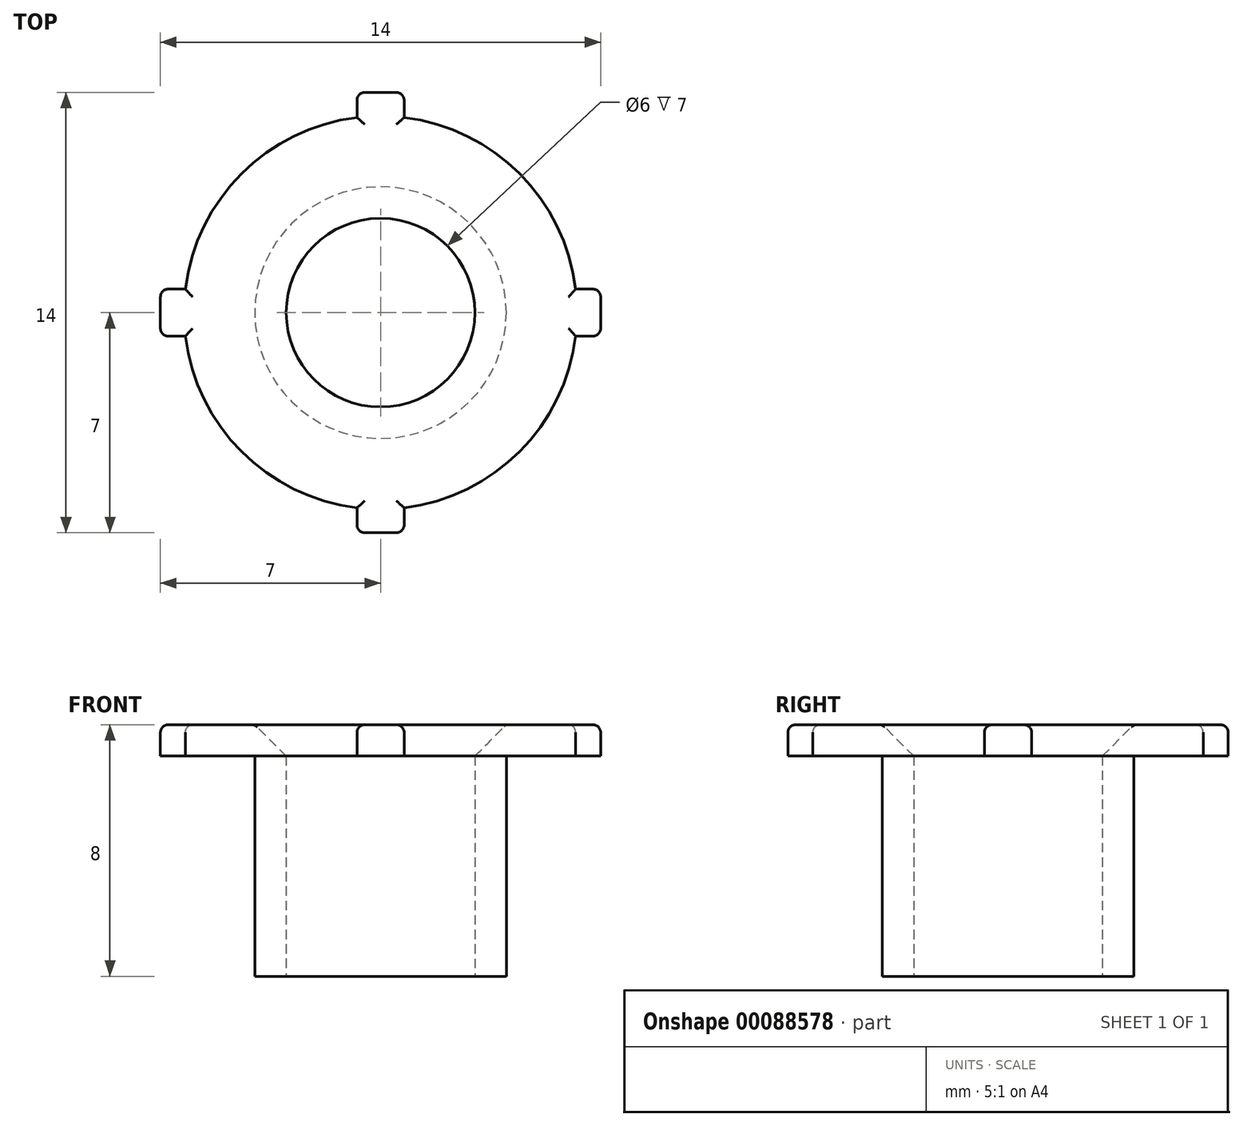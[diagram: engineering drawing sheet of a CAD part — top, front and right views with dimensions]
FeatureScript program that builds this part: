
annotation { "Feature Type Name" : "Feature", "Feature Type Description" : "" }
export const myFeature = defineFeature(function(context is Context, id is Id, definition is map)
    precondition{}
    {
        {
            var Q0;
            Q0=qCreatedBy(makeId("Top.planeOp"),FACE);
            var sketch = newSketch(context, id + "F0", { "sketchPlane" : qUnion([Q0])});
            skCircle(sketch, "E0", {"center": v(0, 0) * mm, "radius": 3 * mm});
            skCircle(sketch, "E1", {"center": v(0, 0) * mm, "radius": 4 * mm});
            skSolve(sketch);
        }
        {
            var Q0;
            Q0=makeQuery(id+"F0.imprint","IMPRINT",FACE,{"disambiguationData":[TD([[makeQuery(id+"F0.imprint","IMPRINT",EDGE,{"derivedFrom":sQuery(id+"F0.wireOp",EDGE,"E0")}),-1.0]])]});
            extrude(context, id + "F1", {"entities" : qUnion([Q0]), "depth" : 7 * mm});
        }
        {
            var Q0;
            Q0=makeQuery(id+"F1.opExtrude","CAP_FACE",FACE,{"disambiguationData":[OSD([sQuery(id+"F0.wireOp",EDGE,"E0"),sQuery(id+"F0.wireOp",EDGE,"E1")])],"isStart":false});
            var sketch = newSketch(context, id + "F2", { "sketchPlane" : qUnion([Q0])});
            skCircle(sketch, "E2", {"center": v(0, 0) * mm, "radius": 3 * mm});
            skCircle(sketch, "E3", {"center": v(0, 0) * mm, "radius": 6.25 * mm});
            skLineSegment(sketch, "E4.rect.bottom", {"start": v(-0.75, -5.5) * mm, "end": v(0.75, -5.5) * mm});
            skLineSegment(sketch, "E4.rect.top", {"start": v(-0.75, -7) * mm, "end": v(0.75, -7) * mm});
            skLineSegment(sketch, "E4.rect.left", {"start": v(-0.75, -5.5) * mm, "end": v(-0.75, -7) * mm});
            skLineSegment(sketch, "E4.rect.right", {"start": v(0.75, -5.5) * mm, "end": v(0.75, -7) * mm});
            skPoint(sketch, "E4.rect.middle", {"position": v(0, -6.25) * mm});
            skLineSegment(sketch, "E5.rect.bottom", {"start": v(-7, 0.75) * mm, "end": v(-5.5, 0.75) * mm});
            skLineSegment(sketch, "E5.rect.top", {"start": v(-7, -0.75) * mm, "end": v(-5.5, -0.75) * mm});
            skLineSegment(sketch, "E5.rect.left", {"start": v(-7, 0.75) * mm, "end": v(-7, -0.75) * mm});
            skLineSegment(sketch, "E5.rect.right", {"start": v(-5.5, 0.75) * mm, "end": v(-5.5, -0.75) * mm});
            skPoint(sketch, "E5.rect.middle", {"position": v(-6.25, 0) * mm});
            skLineSegment(sketch, "E6.MirrorCS", {"start": v(-0.75, 7) * mm, "end": v(0.75, 7) * mm});
            skLineSegment(sketch, "E7.MirrorCS", {"start": v(-0.75, 5.5) * mm, "end": v(-0.75, 7) * mm});
            skLineSegment(sketch, "E8.MirrorCS", {"start": v(0.75, 5.5) * mm, "end": v(0.75, 7) * mm});
            skLineSegment(sketch, "E9.MirrorCS", {"start": v(-0.75, 5.5) * mm, "end": v(0.75, 5.5) * mm});
            skLineSegment(sketch, "E10.MirrorCS", {"start": v(7, 0.75) * mm, "end": v(7, -0.75) * mm});
            skLineSegment(sketch, "E11.MirrorCS", {"start": v(7, -0.75) * mm, "end": v(5.5, -0.75) * mm});
            skLineSegment(sketch, "E12.MirrorCS", {"start": v(7, 0.75) * mm, "end": v(5.5, 0.75) * mm});
            skLineSegment(sketch, "E13.MirrorCS", {"start": v(5.5, 0.75) * mm, "end": v(5.5, -0.75) * mm});
            skSolve(sketch);
        }
        {
            var Q0;
            Q0=qSketchRegion(id+"F2",true);
            extrude(context, id + "F3", {"entities" : qUnion([Q0]), "operationType" : NewBodyOperationType.ADD, "depth" : 1 * mm});
        }
        {
            var Q0;
            Q0=makeQuery(id+"F3.opExtrude","CAP_EDGE",EDGE,{"disambiguationData":[OSD([sQuery(id+"F2.wireOp",EDGE,"E2")])],"isStart":false});
            var Q1;
            Q1=makeQuery(id+"F1.opExtrude","CAP_EDGE",EDGE,{"disambiguationData":[OSD([sQuery(id+"F0.wireOp",EDGE,"E1")])],"isStart":false});
            chamfer(context, id + "F4", {"entities" : qUnion([Q0, Q1]), "width" : 1 * mm, "tangentPropagation" : true});
        }
        {
            var Q0;
            Q0=makeQuery(id+"F3.opExtrude","SWEPT_EDGE",EDGE,{"disambiguationData":[OSD([sQuery(id+"F2.wireOp",EDGE,"E5.rect.top"),sQuery(id+"F2.wireOp",EDGE,"E5.rect.left")])]});
            var Q1;
            Q1=makeQuery(id+"F3.opExtrude","SWEPT_EDGE",EDGE,{"disambiguationData":[OSD([sQuery(id+"F2.wireOp",EDGE,"E5.rect.bottom"),sQuery(id+"F2.wireOp",EDGE,"E5.rect.left")])]});
            var Q2;
            Q2=makeQuery(id+"F3.opExtrude","SWEPT_EDGE",EDGE,{"disambiguationData":[OSD([sQuery(id+"F2.wireOp",EDGE,"E4.rect.top"),sQuery(id+"F2.wireOp",EDGE,"E4.rect.left")])]});
            var Q3;
            Q3=makeQuery(id+"F3.opExtrude","SWEPT_EDGE",EDGE,{"disambiguationData":[OSD([sQuery(id+"F2.wireOp",EDGE,"E4.rect.top"),sQuery(id+"F2.wireOp",EDGE,"E4.rect.right")])]});
            var Q4;
            Q4=makeQuery(id+"F3.opExtrude","SWEPT_EDGE",EDGE,{"disambiguationData":[OSD([sQuery(id+"F2.wireOp",EDGE,"E10.MirrorCS"),sQuery(id+"F2.wireOp",EDGE,"E11.MirrorCS")])]});
            var Q5;
            Q5=makeQuery(id+"F3.opExtrude","SWEPT_EDGE",EDGE,{"disambiguationData":[OSD([sQuery(id+"F2.wireOp",EDGE,"E10.MirrorCS"),sQuery(id+"F2.wireOp",EDGE,"E12.MirrorCS")])]});
            var Q6;
            Q6=makeQuery(id+"F3.opExtrude","SWEPT_EDGE",EDGE,{"disambiguationData":[OSD([sQuery(id+"F2.wireOp",EDGE,"E6.MirrorCS"),sQuery(id+"F2.wireOp",EDGE,"E8.MirrorCS")])]});
            var Q7;
            Q7=makeQuery(id+"F3.opExtrude","SWEPT_EDGE",EDGE,{"disambiguationData":[OSD([sQuery(id+"F2.wireOp",EDGE,"E6.MirrorCS"),sQuery(id+"F2.wireOp",EDGE,"E7.MirrorCS")])]});
            var Q8;
            Q8=makeQuery(id+"F3.opExtrude","CAP_FACE",FACE,{"disambiguationData":[OSD([sQuery(id+"F2.wireOp",EDGE,"E2"),sQuery(id+"F2.wireOp",EDGE,"E4.rect.top"),sQuery(id+"F2.wireOp",EDGE,"E4.rect.left"),sQuery(id+"F2.wireOp",EDGE,"E4.rect.right"),sQuery(id+"F2.wireOp",EDGE,"E5.rect.bottom"),sQuery(id+"F2.wireOp",EDGE,"E5.rect.top"),sQuery(id+"F2.wireOp",EDGE,"E5.rect.left"),sQuery(id+"F2.wireOp",EDGE,"E6.MirrorCS"),sQuery(id+"F2.wireOp",EDGE,"E3"),sQuery(id+"F2.wireOp",EDGE,"E7.MirrorCS"),sQuery(id+"F2.wireOp",EDGE,"E8.MirrorCS"),sQuery(id+"F2.wireOp",EDGE,"E10.MirrorCS"),sQuery(id+"F2.wireOp",EDGE,"E11.MirrorCS"),sQuery(id+"F2.wireOp",EDGE,"E12.MirrorCS")])],"isStart":false});
            fillet(context, id + "F5", {"entities" : qUnion([Q0, Q1, Q2, Q3, Q4, Q5, Q6, Q7, Q8]), "radius" : .25 * mm, "tangentPropagation" : true, "allowEdgeOverflow" : false});
        }
    });
